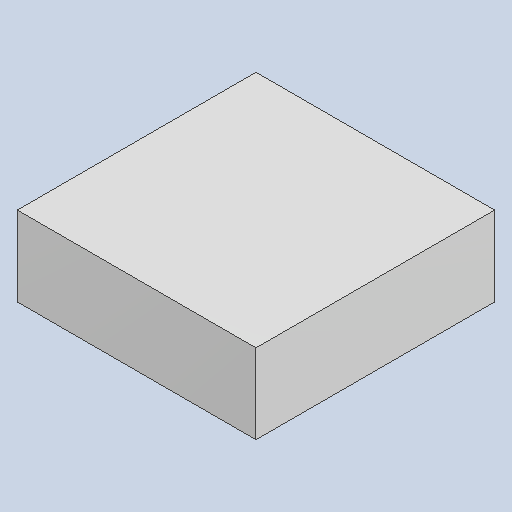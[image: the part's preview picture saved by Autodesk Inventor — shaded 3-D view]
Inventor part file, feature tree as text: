
AUTODESK INVENTOR PART (.ipt)
format: ipt  version: 2023.4 (Build 274418000, 418)  size: 79,872 bytes
history: native  units: mm
features: extrude x1
ambient origin geometry x8: Origin, YZ Plane, XZ Plane, XY Plane, X Axis, Y Axis, Z Axis, Center Point
bodies: Solid1 (feature_tree)
feature tree (1):
  extrude  "Extruded_29"  [1 undecoded]
note: 1 required parameter value undecoded (feature->parameter linkage not recoverable at this tier; creation-order binding heuristic only, values carry confidence <= 0.55)
